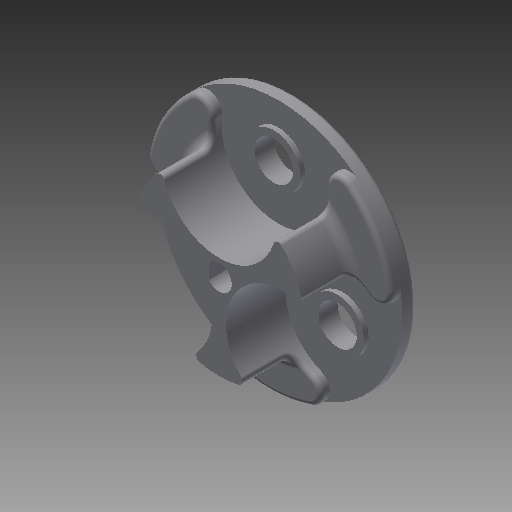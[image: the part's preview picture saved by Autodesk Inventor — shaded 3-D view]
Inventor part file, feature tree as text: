
AUTODESK INVENTOR PART (.ipt)
format: ipt  version: 2022 (Build 260153000, 153)  size: 561,664 bytes
history: native  units: mm
features: other x12, sketch x5, extrude x4, fillet x4, reference x3, mirror x1, pattern_circular x1, revolve x1
ambient origin geometry x8: Origin, YZ Plane, XZ Plane, XY Plane, X Axis, Y Axis, Z Axis, Center Point
bodies: Body1 (feature_tree), Body2 (feature_tree)
feature tree (31):
  other  "Твердое тело1"
  other  "РабПлоскость1"
  extrude  "Выдавливание1"  Depth=0.15mm
  other  "РабПлоскость2"
  extrude  "Выдавливание2"  Depth=22.0mm
  fillet  "Сопряжение1"  Radius=1.0mm
  extrude  "Выдавливание3"  Depth=30.0mm TaperAngle=360.0deg
  mirror  "Зеркальное отражение1"
  extrude  "Выдавливание4"  Depth=31.0mm
  pattern_circular  "Круговой массив1"  [2 undecoded]
  revolve  "Вращение1"
  fillet  "Сопряжение3"  Radius=25.0mm
  other  "Разделение1"
  fillet  "Сопряжение4"  Radius=52.0mm
  fillet  "Сопряжение5"  Radius=3.0mm
  sketch  "Эскиз1"
  reference  "Ссылка1"
  reference  "Ссылка2"
  reference  "Ссылка3"
  sketch  "Эскиз2"
  sketch  "Эскиз3"
  sketch  "Эскиз4"
  sketch  "Эскиз5"
  parser-record x2  (decoder bookkeeping rows leaked as tree rows — omitted from the tree; the rows remain in map.json)
  other  "Nema17.iam"
  other  "Pumpshare:1"
  other  "Shaft:1"
  other  "Твердое тело2"
  other  "Твердое тело3"
  other  "Основание_нижнее:1"
note: 2 required parameter values undecoded (feature->parameter linkage not recoverable at this tier; creation-order binding heuristic only, values carry confidence <= 0.55)
note: 2 file-system paths scrubbed to <path> (originals preserved in map.json)
